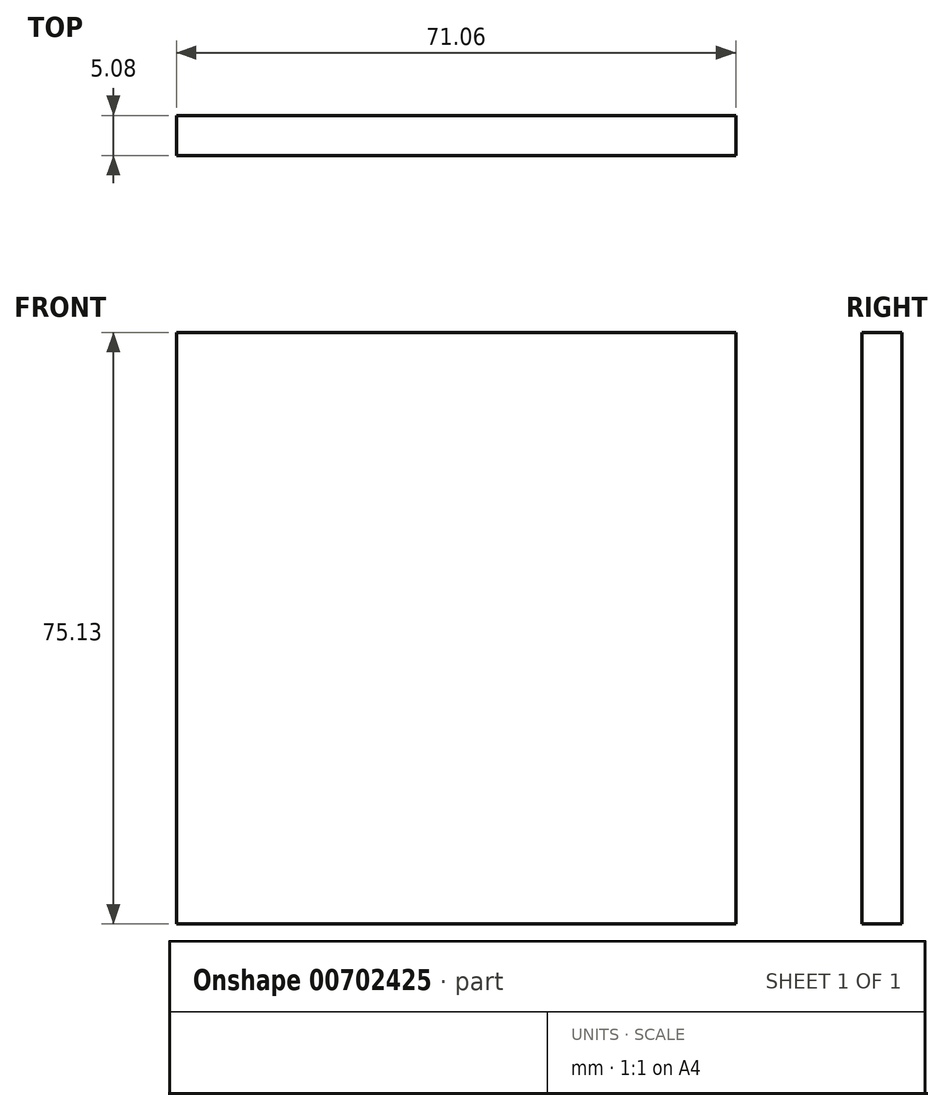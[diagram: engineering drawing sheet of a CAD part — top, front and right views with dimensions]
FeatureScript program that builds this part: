
annotation { "Feature Type Name" : "Feature", "Feature Type Description" : "" }
export const myFeature = defineFeature(function(context is Context, id is Id, definition is map)
    precondition{}
    {
        {
            var Q0;
            Q0=qCreatedBy(makeId("Front.planeOp"),FACE);
            var sketch = newSketch(context, id + "F0", { "sketchPlane" : qUnion([Q0])});
            skLineSegment(sketch, "E0.top", {"start": v(35.53, 49.38) * mm, "end": v(-35.53, 49.38) * mm});
            skLineSegment(sketch, "E0.left", {"start": v(35.53, -25.75) * mm, "end": v(35.53, 49.38) * mm});
            skLineSegment(sketch, "E0.right", {"start": v(-35.53, -25.75) * mm, "end": v(-35.53, 49.38) * mm});
            skPoint(sketch, "E0.middle", {"position": v(0, 0) * mm});
            skPoint(sketch, "E1.orphan", {"position": v(-35.53, -49.38) * mm});
            skPoint(sketch, "E2.orphan", {"position": v(35.53, -49.38) * mm});
            skLineSegment(sketch, "E3", {"start": v(-35.53, -25.75) * mm, "end": v(35.53, -25.75) * mm});
            skSolve(sketch);
        }
        {
            var Q0;
            Q0=qSketchRegion(id+"F0",true);
            extrude(context, id + "F1", {"entities" : qUnion([Q0]), "depth" : 5.08 * mm, "offsetDistance" : 25.4 * mm});
        }
    });
